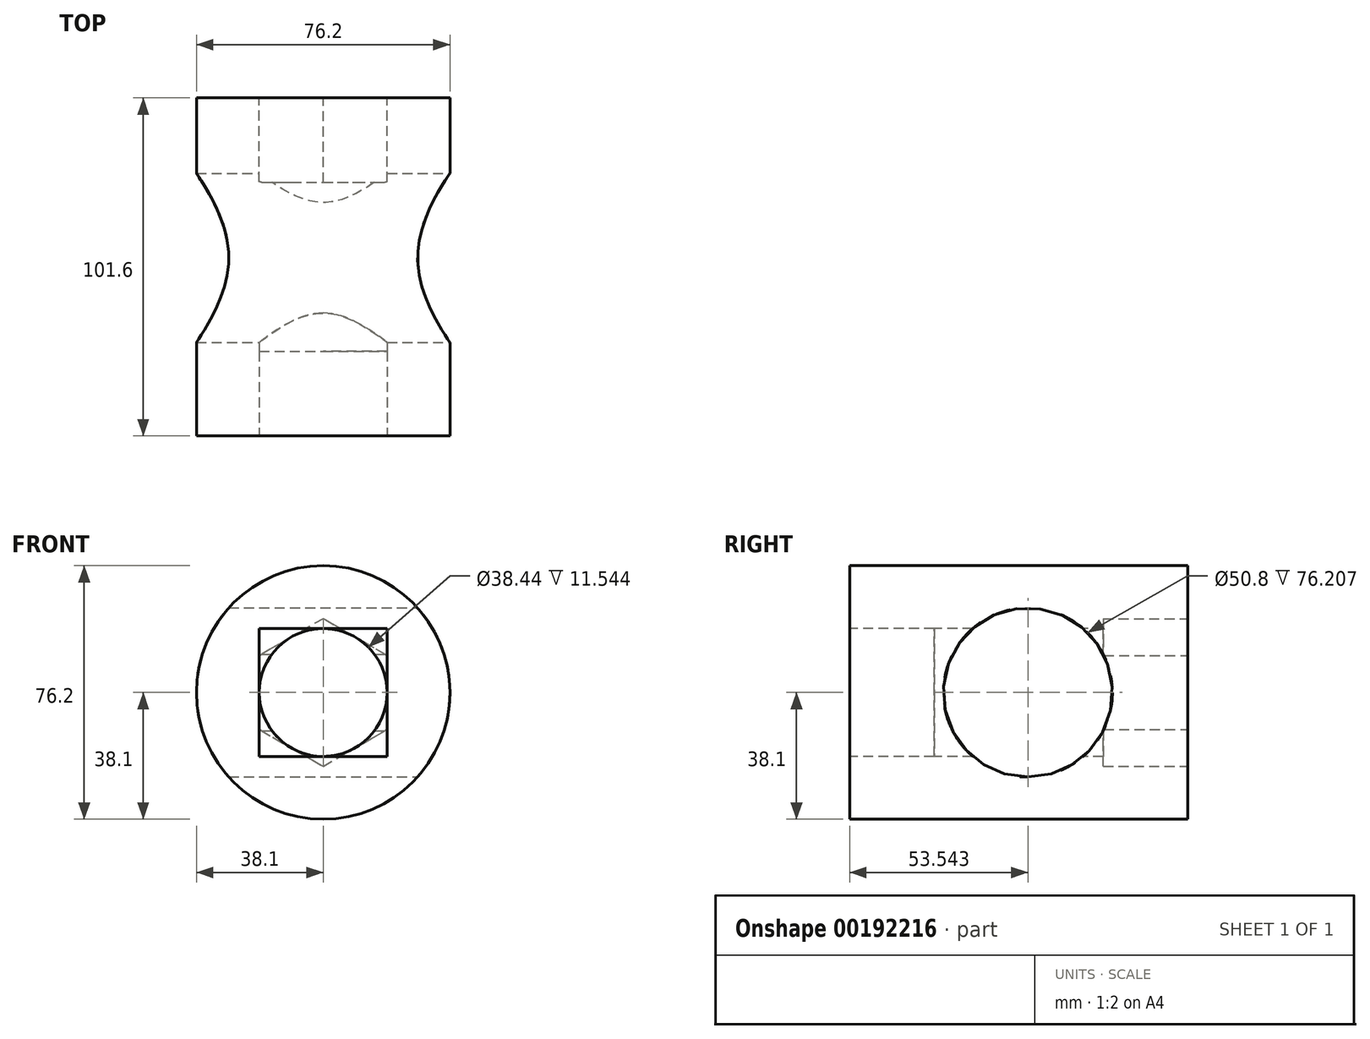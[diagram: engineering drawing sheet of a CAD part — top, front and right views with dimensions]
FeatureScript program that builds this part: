
annotation { "Feature Type Name" : "Feature", "Feature Type Description" : "" }
export const myFeature = defineFeature(function(context is Context, id is Id, definition is map)
    precondition{}
    {
        {
            var Q0;
            Q0=qCreatedBy(makeId("Front.planeOp"),FACE);
            var sketch = newSketch(context, id + "F0", { "sketchPlane" : qUnion([Q0])});
            skCircle(sketch, "E0", {"center": v(0, 0) * mm, "radius": 38.1 * mm});
            skLineSegment(sketch, "E1.bottom", {"start": v(-19.22, -19.22) * mm, "end": v(19.22, -19.22) * mm});
            skLineSegment(sketch, "E1.top", {"start": v(-19.22, 19.22) * mm, "end": v(19.22, 19.22) * mm});
            skLineSegment(sketch, "E1.left", {"start": v(-19.22, -19.22) * mm, "end": v(-19.22, 19.22) * mm});
            skLineSegment(sketch, "E1.right", {"start": v(19.22, -19.22) * mm, "end": v(19.22, 19.22) * mm});
            skCircle(sketch, "E2", {"center": v(0, 0) * mm, "radius": 19.22 * mm});
            skSolve(sketch);
        }
        {
            var Q0;
            Q0=makeQuery(id+"F0.imprint","IMPRINT",FACE,{"disambiguationData":[TD([[makeQuery(id+"F0.imprint","IMPRINT",EDGE,{"derivedFrom":sQuery(id+"F0.wireOp",EDGE,"E0")}),1.0]])]});
            var Q1;
            {var subQ0=sQuery(id+"F0.wireOp",EDGE,"E1.right");var subQ1=sQuery(id+"F0.wireOp",EDGE,"E1.top");var subQ2=makeQuery(id+"F0.imprint","INTERSECT",VERTEX,{"derivedFrom":[subQ1,subQ0]});Q1=makeQuery(id+"F0.imprint","IMPRINT",FACE,{"disambiguationData":[TD([[makeQuery(id+"F0.imprint","IMPRINT",EDGE,{"disambiguationData":[TD([[subQ2,1.0]])],"derivedFrom":subQ1}),-1.0]])]});}
            var Q2;
            {var subQ0=sQuery(id+"F0.wireOp",EDGE,"E2");var subQ1=makeQuery(id+"F0.imprint","INTERSECT",VERTEX,{"derivedFrom":[sQuery(id+"F0.wireOp",EDGE,"E1.top"),subQ0]});Q2=makeQuery(id+"F0.imprint","IMPRINT",FACE,{"disambiguationData":[TD([[makeQuery(id+"F0.imprint","IMPRINT",EDGE,{"disambiguationData":[TD([[subQ1,1.0]])],"derivedFrom":subQ0}),1.0]])]});}
            var Q3;
            {var subQ0=sQuery(id+"F0.wireOp",EDGE,"E1.left");var subQ1=sQuery(id+"F0.wireOp",EDGE,"E1.top");var subQ2=makeQuery(id+"F0.imprint","INTERSECT",VERTEX,{"derivedFrom":[subQ1,subQ0]});Q3=makeQuery(id+"F0.imprint","IMPRINT",FACE,{"disambiguationData":[TD([[makeQuery(id+"F0.imprint","IMPRINT",EDGE,{"disambiguationData":[TD([[subQ2,-1.0]])],"derivedFrom":subQ1}),-1.0]])]});}
            var Q4;
            {var subQ0=sQuery(id+"F0.wireOp",EDGE,"E1.left");var subQ1=sQuery(id+"F0.wireOp",EDGE,"E1.bottom");var subQ2=makeQuery(id+"F0.imprint","INTERSECT",VERTEX,{"derivedFrom":[subQ1,subQ0]});Q4=makeQuery(id+"F0.imprint","IMPRINT",FACE,{"disambiguationData":[TD([[makeQuery(id+"F0.imprint","IMPRINT",EDGE,{"disambiguationData":[TD([[subQ2,-1.0]])],"derivedFrom":subQ1}),1.0]])]});}
            var Q5;
            {var subQ0=sQuery(id+"F0.wireOp",EDGE,"E1.right");var subQ1=sQuery(id+"F0.wireOp",EDGE,"E1.bottom");var subQ2=makeQuery(id+"F0.imprint","INTERSECT",VERTEX,{"derivedFrom":[subQ1,subQ0]});Q5=makeQuery(id+"F0.imprint","IMPRINT",FACE,{"disambiguationData":[TD([[makeQuery(id+"F0.imprint","IMPRINT",EDGE,{"disambiguationData":[TD([[subQ2,1.0]])],"derivedFrom":subQ1}),1.0]])]});}
            extrude(context, id + "F1", {"entities" : qUnion([Q0, Q1, Q2, Q3, Q4, Q5]), "oppositeDirection" : true, "depth" : 101.6 * mm});
        }
        {
            var Q0;
            {var subQ0=sQuery(id+"F0.wireOp",EDGE,"E2");var subQ1=makeQuery(id+"F0.imprint","INTERSECT",VERTEX,{"derivedFrom":[sQuery(id+"F0.wireOp",EDGE,"E1.top"),subQ0]});Q0=makeQuery(id+"F0.imprint","IMPRINT",FACE,{"disambiguationData":[TD([[makeQuery(id+"F0.imprint","IMPRINT",EDGE,{"disambiguationData":[TD([[subQ1,1.0]])],"derivedFrom":subQ0}),1.0]])]});}
            extrude(context, id + "F2", {"entities" : qUnion([Q0]), "operationType" : NewBodyOperationType.REMOVE, "endBound" : BoundingType.THROUGH_ALL, "oppositeDirection" : true, "depth" : 25.4 * mm});
        }
        {
            var Q0;
            {var subQ0=sQuery(id+"F0.wireOp",EDGE,"E1.right");var subQ1=sQuery(id+"F0.wireOp",EDGE,"E1.bottom");var subQ2=makeQuery(id+"F0.imprint","INTERSECT",VERTEX,{"derivedFrom":[subQ1,subQ0]});Q0=makeQuery(id+"F0.imprint","IMPRINT",FACE,{"disambiguationData":[TD([[makeQuery(id+"F0.imprint","IMPRINT",EDGE,{"disambiguationData":[TD([[subQ2,1.0]])],"derivedFrom":subQ1}),1.0]])]});}
            var Q1;
            {var subQ0=sQuery(id+"F0.wireOp",EDGE,"E1.left");var subQ1=sQuery(id+"F0.wireOp",EDGE,"E1.bottom");var subQ2=makeQuery(id+"F0.imprint","INTERSECT",VERTEX,{"derivedFrom":[subQ1,subQ0]});Q1=makeQuery(id+"F0.imprint","IMPRINT",FACE,{"disambiguationData":[TD([[makeQuery(id+"F0.imprint","IMPRINT",EDGE,{"disambiguationData":[TD([[subQ2,-1.0]])],"derivedFrom":subQ1}),1.0]])]});}
            var Q2;
            {var subQ0=sQuery(id+"F0.wireOp",EDGE,"E1.left");var subQ1=sQuery(id+"F0.wireOp",EDGE,"E1.top");var subQ2=makeQuery(id+"F0.imprint","INTERSECT",VERTEX,{"derivedFrom":[subQ1,subQ0]});Q2=makeQuery(id+"F0.imprint","IMPRINT",FACE,{"disambiguationData":[TD([[makeQuery(id+"F0.imprint","IMPRINT",EDGE,{"disambiguationData":[TD([[subQ2,-1.0]])],"derivedFrom":subQ1}),-1.0]])]});}
            var Q3;
            {var subQ0=sQuery(id+"F0.wireOp",EDGE,"E1.right");var subQ1=sQuery(id+"F0.wireOp",EDGE,"E1.top");var subQ2=makeQuery(id+"F0.imprint","INTERSECT",VERTEX,{"derivedFrom":[subQ1,subQ0]});Q3=makeQuery(id+"F0.imprint","IMPRINT",FACE,{"disambiguationData":[TD([[makeQuery(id+"F0.imprint","IMPRINT",EDGE,{"disambiguationData":[TD([[subQ2,1.0]])],"derivedFrom":subQ1}),-1.0]])]});}
            extrude(context, id + "F3", {"entities" : qUnion([Q0, Q1, Q2, Q3]), "operationType" : NewBodyOperationType.REMOVE, "oppositeDirection" : true, "depth" : 25.4 * mm});
        }
        {
            var Q0;
            Q0=makeQuery(id+"F1.opExtrude","CAP_FACE",FACE,{"disambiguationData":[OSD([sQuery(id+"F0.wireOp",EDGE,"E0")])],"isStart":false});
            var sketch = newSketch(context, id + "F4", { "sketchPlane" : qUnion([Q0])});
            skCircle(sketch, "E3.cCircle", {"center": v(0, 0) * mm, "radius": 19.22 * mm, "construction": true});
            skLineSegment(sketch, "E3.0", {"start": v(-19.22, -11.1) * mm, "end": v(-19.22, 11.1) * mm});
            skLineSegment(sketch, "E3.1", {"start": v(-19.22, 11.1) * mm, "end": v(0, 22.2) * mm});
            skLineSegment(sketch, "E3.2", {"start": v(0, 22.2) * mm, "end": v(19.22, 11.1) * mm});
            skLineSegment(sketch, "E3.3", {"start": v(19.22, 11.1) * mm, "end": v(19.22, -11.1) * mm});
            skLineSegment(sketch, "E3.4", {"start": v(19.22, -11.1) * mm, "end": v(0, -22.2) * mm});
            skLineSegment(sketch, "E3.5", {"start": v(0, -22.2) * mm, "end": v(-19.22, -11.1) * mm});
            skPoint(sketch, "E3.0.midPoint", {"position": v(-19.22, 0) * mm});
            skSolve(sketch);
        }
        {
            var Q0;
            Q0 = qSketchRegion(id + "F4", true);
            extrude(context, id + "F5", {"entities" : qUnion([Q0]), "operationType" : NewBodyOperationType.REMOVE, "oppositeDirection" : true, "depth" : 25.4 * mm});
        }
        {
            var Q0;
            Q0=qCreatedBy(makeId("Right.planeOp"),FACE);
            var sketch = newSketch(context, id + "F6", { "sketchPlane" : qUnion([Q0])});
            skCircle(sketch, "E4", {"center": v(53.54, 0) * mm, "radius": 25.4 * mm});
            skSolve(sketch);
        }
        {
            var Q0;
            Q0 = qSketchRegion(id + "F6", true);
            extrude(context, id + "F7", {"entities" : qUnion([Q0]), "operationType" : NewBodyOperationType.REMOVE, "endBound" : BoundingType.SYMMETRIC, "oppositeDirection" : true, "depth" : 76.2 * mm});
        }
    });
